# Revit family: VLMF-KARO-S-2500-xxx-F-SWx
name_source: partatom
category: Oprawy oświetleniowe
units: mm (PartAtom-declared; Revit-internal decimal feet)

## family parameters
Numer OmniClass = 23.80.70.11
Obiekt nadrzędny = Powierzchnia
Punkt obliczania pomieszczeń = Nie
Tnij formami wycięć po wczytaniu = Nie
Typ części = Normalny
Tytuł OmniClass = Luminaries for Internal Lighting
Współdzielony = Nie
Wymiar okrągłego złącza = Użyj średnicy
Źródło światła = Tak

## types (4) — shared parameters
Emituj kształt widoczny w renderingu = Nie
Emituj z długości prostokąta = 95 mm  [stored 0.31168 ft]
Emituj z szerokości prostokąta = 95 mm  [stored 0.31168 ft]
Filtr koloru = 16777215
Kod zespołu = D5020200
Lampa = LED
Obciążenie pozorne = 27 VA
Odchylenie kierunku = 90.00°
Plik sieci fotometrycznej = KARO-S 2500-840 F.IES
Producent = RIDI Leuchten GmbH
URL = www.ridi.de
Zmiana temperatury barwowej przyciemniania lampy = <Brak>
brand = RIDI
conformity mark = CE
electrical safety class = 1
height = 166 mm  [stored 0.544619 ft]
ingress protection (IP) code = IP20
length = 500 mm  [stored 1.64042 ft]
nominal frequency = 50-60Hz
nominal voltage = 230
rated input power = 27
voltage type (AC, DC, UC) = AC
weight = 1,125kg
width = 67 mm
zero-valued in all types: Domyślna rzędna

## per-type parameters (varying)
| type | Model | product name |
| VLMF-KARO-S 2500-830 F-SW | 0321893SW691 | VLMF-KARO-S 2500-830 F-SW |
| VLMF-KARO-S 2500-830 F-SW-DA | 0331893SW691 | VLMF-KARO-S 2500-830 F-SW-DA |
| VLMF-KARO-S 2500-840 F-SW | 0321886SW691 | VLMF-KARO-S 2500-830 F-SW-DA |
| VLMF-KARO-S 2500-840 F-SW-DA | 0331886SW691 | VLMF-KARO-S 2500-840 F-SW-DA |

note: [stored X ft] marks values corroborated as IEEE doubles in the binary element streams (Revit-internal decimal feet)
